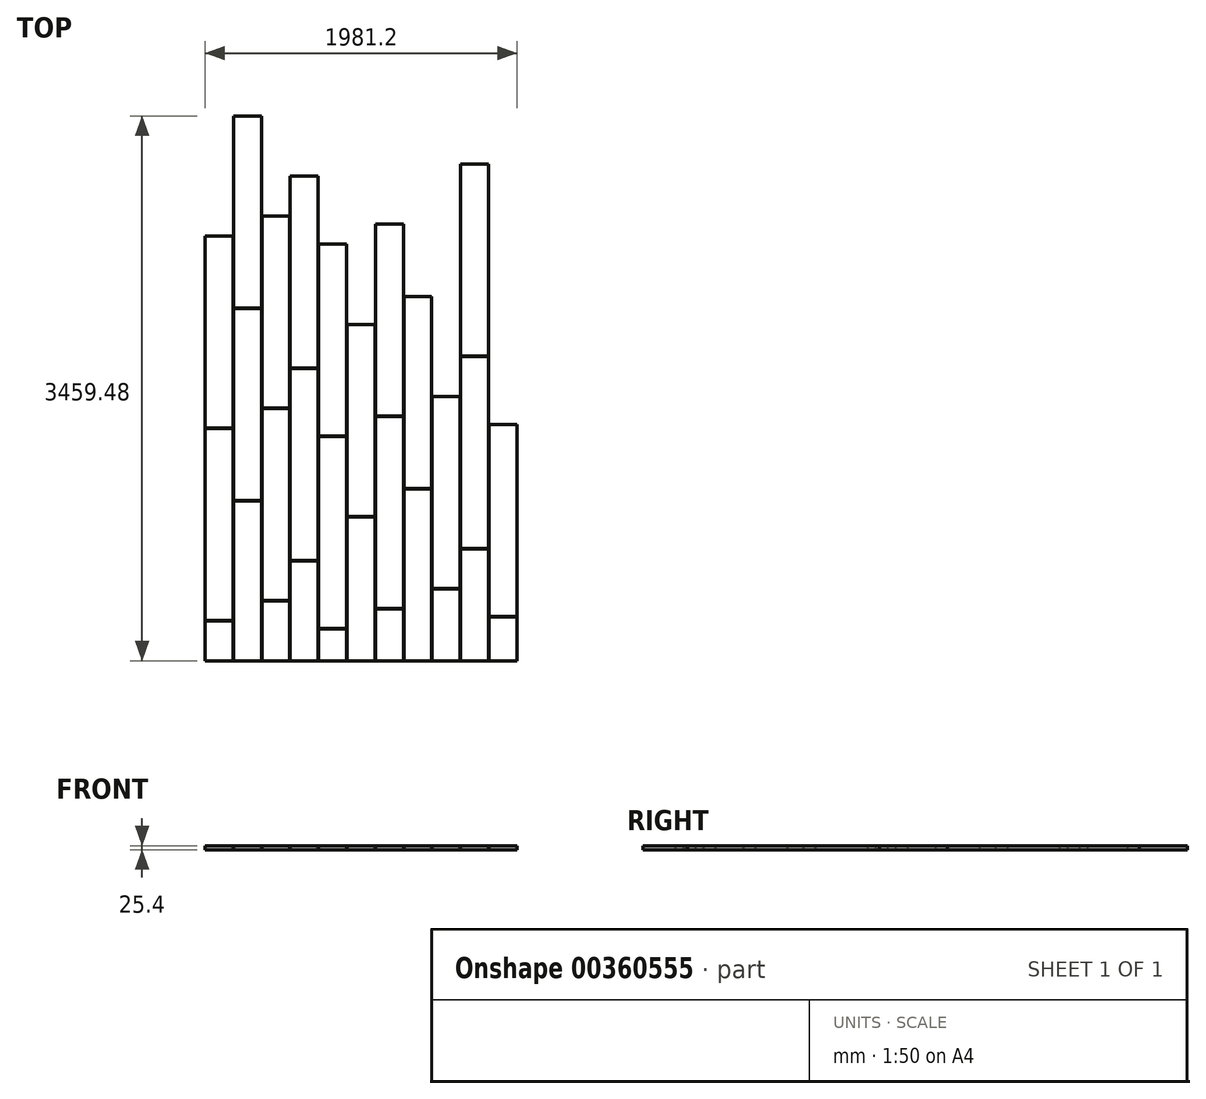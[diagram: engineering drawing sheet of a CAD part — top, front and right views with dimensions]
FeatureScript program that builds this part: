
annotation { "Feature Type Name" : "Feature", "Feature Type Description" : "" }
export const myFeature = defineFeature(function(context is Context, id is Id, definition is map)
    precondition{}
    {
        {
            var Q0;
            Q0=qCreatedBy(makeId("Top.planeOp"),FACE);
            var sketch = newSketch(context, id + "F0", { "sketchPlane" : qUnion([Q0])});
            skLineSegment(sketch, "E0.bottom", {"start": v(0, 0) * mm, "end": v(177.8, 0) * mm});
            skLineSegment(sketch, "E0.top", {"start": v(0, 254) * mm, "end": v(177.8, 254) * mm});
            skLineSegment(sketch, "E0.left", {"start": v(0, 0) * mm, "end": v(0, 254) * mm});
            skLineSegment(sketch, "E0.right", {"start": v(177.8, 0) * mm, "end": v(177.8, 254) * mm});
            skLineSegment(sketch, "E1.bottom", {"start": v(180.34, 0) * mm, "end": v(358.14, 0) * mm});
            skLineSegment(sketch, "E1.top", {"start": v(180.34, 1016) * mm, "end": v(358.14, 1016) * mm});
            skLineSegment(sketch, "E1.left", {"start": v(180.34, 0) * mm, "end": v(180.34, 1016) * mm});
            skLineSegment(sketch, "E1.right", {"start": v(358.14, 0) * mm, "end": v(358.14, 1016) * mm});
            skLineSegment(sketch, "E2.bottom", {"start": v(360.68, 0) * mm, "end": v(538.48, 0) * mm});
            skLineSegment(sketch, "E2.top", {"start": v(360.68, 381) * mm, "end": v(538.48, 381) * mm});
            skLineSegment(sketch, "E2.left", {"start": v(360.68, 0) * mm, "end": v(360.68, 381) * mm});
            skLineSegment(sketch, "E2.right", {"start": v(538.48, 0) * mm, "end": v(538.48, 381) * mm});
            skLineSegment(sketch, "E3.bottom", {"start": v(541.02, 0) * mm, "end": v(718.82, 0) * mm});
            skLineSegment(sketch, "E3.top", {"start": v(541.02, 635) * mm, "end": v(718.82, 635) * mm});
            skLineSegment(sketch, "E3.left", {"start": v(541.02, 0) * mm, "end": v(541.02, 635) * mm});
            skLineSegment(sketch, "E3.right", {"start": v(718.82, 0) * mm, "end": v(718.82, 635) * mm});
            skLineSegment(sketch, "E4.bottom", {"start": v(721.36, 0) * mm, "end": v(899.16, 0) * mm});
            skLineSegment(sketch, "E4.top", {"start": v(721.36, 203.2) * mm, "end": v(899.16, 203.2) * mm});
            skLineSegment(sketch, "E4.left", {"start": v(721.36, 0) * mm, "end": v(721.36, 203.2) * mm});
            skLineSegment(sketch, "E4.right", {"start": v(899.16, 0) * mm, "end": v(899.16, 203.2) * mm});
            skLineSegment(sketch, "E5.bottom", {"start": v(0, 256.54) * mm, "end": v(177.8, 256.54) * mm});
            skLineSegment(sketch, "E5.top", {"start": v(0, 1475.74) * mm, "end": v(177.8, 1475.74) * mm});
            skLineSegment(sketch, "E5.left", {"start": v(0, 256.54) * mm, "end": v(0, 1475.74) * mm});
            skLineSegment(sketch, "E5.right", {"start": v(177.8, 256.54) * mm, "end": v(177.8, 1475.74) * mm});
            skLineSegment(sketch, "E6.bottom", {"start": v(180.34, 1018.54) * mm, "end": v(358.14, 1018.54) * mm});
            skLineSegment(sketch, "E6.top", {"start": v(180.34, 2237.74) * mm, "end": v(358.14, 2237.74) * mm});
            skLineSegment(sketch, "E6.left", {"start": v(180.34, 1018.54) * mm, "end": v(180.34, 2237.74) * mm});
            skLineSegment(sketch, "E6.right", {"start": v(358.14, 1018.54) * mm, "end": v(358.14, 2237.74) * mm});
            skLineSegment(sketch, "E7.bottom", {"start": v(360.68, 383.54) * mm, "end": v(538.48, 383.54) * mm});
            skLineSegment(sketch, "E7.top", {"start": v(360.68, 1602.74) * mm, "end": v(538.48, 1602.74) * mm});
            skLineSegment(sketch, "E7.left", {"start": v(360.68, 383.54) * mm, "end": v(360.68, 1602.74) * mm});
            skLineSegment(sketch, "E7.right", {"start": v(538.48, 383.54) * mm, "end": v(538.48, 1602.74) * mm});
            skLineSegment(sketch, "E8.bottom", {"start": v(541.02, 637.54) * mm, "end": v(718.82, 637.54) * mm});
            skLineSegment(sketch, "E8.top", {"start": v(541.02, 1856.74) * mm, "end": v(718.82, 1856.74) * mm});
            skLineSegment(sketch, "E8.left", {"start": v(541.02, 637.54) * mm, "end": v(541.02, 1856.74) * mm});
            skLineSegment(sketch, "E8.right", {"start": v(718.82, 637.54) * mm, "end": v(718.82, 1856.74) * mm});
            skLineSegment(sketch, "E9.bottom", {"start": v(721.36, 205.74) * mm, "end": v(899.16, 205.74) * mm});
            skLineSegment(sketch, "E9.top", {"start": v(721.36, 1424.94) * mm, "end": v(899.16, 1424.94) * mm});
            skLineSegment(sketch, "E9.left", {"start": v(721.36, 205.74) * mm, "end": v(721.36, 1424.94) * mm});
            skLineSegment(sketch, "E9.right", {"start": v(899.16, 205.74) * mm, "end": v(899.16, 1424.94) * mm});
            skLineSegment(sketch, "E10.bottom", {"start": v(0, 1478.28) * mm, "end": v(177.8, 1478.28) * mm});
            skLineSegment(sketch, "E10.top", {"start": v(0, 2697.48) * mm, "end": v(177.8, 2697.48) * mm});
            skLineSegment(sketch, "E10.left", {"start": v(0, 1478.28) * mm, "end": v(0, 2697.48) * mm});
            skLineSegment(sketch, "E10.right", {"start": v(177.8, 1478.28) * mm, "end": v(177.8, 2697.48) * mm});
            skPoint(sketch, "E11.firstSnap0", {"position": v(180.34, 1628.14) * mm});
            skLineSegment(sketch, "E11.bottom", {"start": v(180.34, 2240.28) * mm, "end": v(358.14, 2240.28) * mm});
            skLineSegment(sketch, "E11.top", {"start": v(180.34, 3459.48) * mm, "end": v(358.14, 3459.48) * mm});
            skLineSegment(sketch, "E11.left", {"start": v(180.34, 2240.28) * mm, "end": v(180.34, 3459.48) * mm});
            skLineSegment(sketch, "E11.right", {"start": v(358.14, 2240.28) * mm, "end": v(358.14, 3459.48) * mm});
            skLineSegment(sketch, "E12.bottom", {"start": v(360.68, 1605.28) * mm, "end": v(538.48, 1605.28) * mm});
            skLineSegment(sketch, "E12.top", {"start": v(360.68, 2824.48) * mm, "end": v(538.48, 2824.48) * mm});
            skLineSegment(sketch, "E12.left", {"start": v(360.68, 1605.28) * mm, "end": v(360.68, 2824.48) * mm});
            skLineSegment(sketch, "E12.right", {"start": v(538.48, 1605.28) * mm, "end": v(538.48, 2824.48) * mm});
            skLineSegment(sketch, "E13.bottom", {"start": v(541.02, 1859.28) * mm, "end": v(718.82, 1859.28) * mm});
            skLineSegment(sketch, "E13.top", {"start": v(541.02, 3078.48) * mm, "end": v(718.82, 3078.48) * mm});
            skLineSegment(sketch, "E13.left", {"start": v(541.02, 1859.28) * mm, "end": v(541.02, 3078.48) * mm});
            skLineSegment(sketch, "E13.right", {"start": v(718.82, 1859.28) * mm, "end": v(718.82, 3078.48) * mm});
            skPoint(sketch, "E14.oppositeSnap0", {"position": v(899.16, 815.34) * mm});
            skLineSegment(sketch, "E14.bottom", {"start": v(721.36, 1427.48) * mm, "end": v(899.16, 1427.48) * mm});
            skLineSegment(sketch, "E14.top", {"start": v(721.36, 2646.68) * mm, "end": v(899.16, 2646.68) * mm});
            skLineSegment(sketch, "E14.left", {"start": v(721.36, 1427.48) * mm, "end": v(721.36, 2646.68) * mm});
            skLineSegment(sketch, "E14.right", {"start": v(899.16, 1427.48) * mm, "end": v(899.16, 2646.68) * mm});
            skLineSegment(sketch, "E15.bottom", {"start": v(901.7, 0) * mm, "end": v(1079.5, 0) * mm});
            skLineSegment(sketch, "E15.top", {"start": v(901.7, 914.4) * mm, "end": v(1079.5, 914.4) * mm});
            skLineSegment(sketch, "E15.left", {"start": v(901.7, 0) * mm, "end": v(901.7, 914.4) * mm});
            skLineSegment(sketch, "E15.right", {"start": v(1079.5, 0) * mm, "end": v(1079.5, 914.4) * mm});
            skLineSegment(sketch, "E16.bottom", {"start": v(901.7, 916.94) * mm, "end": v(1079.5, 916.94) * mm});
            skLineSegment(sketch, "E16.top", {"start": v(901.7, 2136.14) * mm, "end": v(1079.5, 2136.14) * mm});
            skLineSegment(sketch, "E16.left", {"start": v(901.7, 916.94) * mm, "end": v(901.7, 2136.14) * mm});
            skLineSegment(sketch, "E16.right", {"start": v(1079.5, 916.94) * mm, "end": v(1079.5, 2136.14) * mm});
            skLineSegment(sketch, "E17.bottom", {"start": v(1082.04, 0) * mm, "end": v(1259.84, 0) * mm});
            skLineSegment(sketch, "E17.top", {"start": v(1082.04, 330.2) * mm, "end": v(1259.84, 330.2) * mm});
            skLineSegment(sketch, "E17.left", {"start": v(1082.04, 0) * mm, "end": v(1082.04, 330.2) * mm});
            skLineSegment(sketch, "E17.right", {"start": v(1259.84, 0) * mm, "end": v(1259.84, 330.2) * mm});
            skLineSegment(sketch, "E18.bottom", {"start": v(1262.38, 0) * mm, "end": v(1440.18, 0) * mm});
            skLineSegment(sketch, "E18.top", {"start": v(1262.38, 1092.2) * mm, "end": v(1440.18, 1092.2) * mm});
            skLineSegment(sketch, "E18.left", {"start": v(1262.38, 0) * mm, "end": v(1262.38, 1092.2) * mm});
            skLineSegment(sketch, "E18.right", {"start": v(1440.18, 0) * mm, "end": v(1440.18, 1092.2) * mm});
            skLineSegment(sketch, "E19.bottom", {"start": v(1082.04, 332.74) * mm, "end": v(1259.84, 332.74) * mm});
            skLineSegment(sketch, "E19.top", {"start": v(1082.04, 1551.94) * mm, "end": v(1259.84, 1551.94) * mm});
            skLineSegment(sketch, "E19.left", {"start": v(1082.04, 332.74) * mm, "end": v(1082.04, 1551.94) * mm});
            skLineSegment(sketch, "E19.right", {"start": v(1259.84, 332.74) * mm, "end": v(1259.84, 1551.94) * mm});
            skLineSegment(sketch, "E20.bottom", {"start": v(1442.72, 0) * mm, "end": v(1620.52, 0) * mm});
            skLineSegment(sketch, "E20.top", {"start": v(1442.72, 457.2) * mm, "end": v(1620.52, 457.2) * mm});
            skLineSegment(sketch, "E20.left", {"start": v(1442.72, 0) * mm, "end": v(1442.72, 457.2) * mm});
            skLineSegment(sketch, "E20.right", {"start": v(1620.52, 0) * mm, "end": v(1620.52, 457.2) * mm});
            skLineSegment(sketch, "E21.bottom", {"start": v(1623.06, 0) * mm, "end": v(1800.86, 0) * mm});
            skLineSegment(sketch, "E21.top", {"start": v(1623.06, 711.2) * mm, "end": v(1800.86, 711.2) * mm});
            skLineSegment(sketch, "E21.left", {"start": v(1623.06, 0) * mm, "end": v(1623.06, 711.2) * mm});
            skLineSegment(sketch, "E21.right", {"start": v(1800.86, 0) * mm, "end": v(1800.86, 711.2) * mm});
            skLineSegment(sketch, "E22.bottom", {"start": v(1442.72, 459.74) * mm, "end": v(1620.52, 459.74) * mm});
            skLineSegment(sketch, "E22.top", {"start": v(1442.72, 1678.94) * mm, "end": v(1620.52, 1678.94) * mm});
            skLineSegment(sketch, "E22.left", {"start": v(1442.72, 459.74) * mm, "end": v(1442.72, 1678.94) * mm});
            skLineSegment(sketch, "E22.right", {"start": v(1620.52, 459.74) * mm, "end": v(1620.52, 1678.94) * mm});
            skLineSegment(sketch, "E23.bottom", {"start": v(1623.06, 713.74) * mm, "end": v(1800.86, 713.74) * mm});
            skLineSegment(sketch, "E23.top", {"start": v(1623.06, 1932.94) * mm, "end": v(1800.86, 1932.94) * mm});
            skLineSegment(sketch, "E23.left", {"start": v(1623.06, 713.74) * mm, "end": v(1623.06, 1932.94) * mm});
            skLineSegment(sketch, "E23.right", {"start": v(1800.86, 713.74) * mm, "end": v(1800.86, 1932.94) * mm});
            skLineSegment(sketch, "E24.bottom", {"start": v(1082.04, 1554.48) * mm, "end": v(1259.84, 1554.48) * mm});
            skLineSegment(sketch, "E24.top", {"start": v(1082.04, 2773.68) * mm, "end": v(1259.84, 2773.68) * mm});
            skLineSegment(sketch, "E24.left", {"start": v(1082.04, 1554.48) * mm, "end": v(1082.04, 2773.68) * mm});
            skLineSegment(sketch, "E24.right", {"start": v(1259.84, 1554.48) * mm, "end": v(1259.84, 2773.68) * mm});
            skLineSegment(sketch, "E25.bottom", {"start": v(1262.38, 1094.74) * mm, "end": v(1440.18, 1094.74) * mm});
            skLineSegment(sketch, "E25.top", {"start": v(1262.38, 2313.94) * mm, "end": v(1440.18, 2313.94) * mm});
            skLineSegment(sketch, "E25.left", {"start": v(1262.38, 1094.74) * mm, "end": v(1262.38, 2313.94) * mm});
            skLineSegment(sketch, "E25.right", {"start": v(1440.18, 1094.74) * mm, "end": v(1440.18, 2313.94) * mm});
            skLineSegment(sketch, "E26.bottom", {"start": v(1623.06, 1935.48) * mm, "end": v(1800.86, 1935.48) * mm});
            skLineSegment(sketch, "E26.top", {"start": v(1623.06, 3154.68) * mm, "end": v(1800.86, 3154.68) * mm});
            skLineSegment(sketch, "E26.left", {"start": v(1623.06, 1935.48) * mm, "end": v(1623.06, 3154.68) * mm});
            skLineSegment(sketch, "E26.right", {"start": v(1800.86, 1935.48) * mm, "end": v(1800.86, 3154.68) * mm});
            skLineSegment(sketch, "E27.bottom", {"start": v(1803.4, 0) * mm, "end": v(1981.2, 0) * mm});
            skLineSegment(sketch, "E27.top", {"start": v(1803.4, 279.4) * mm, "end": v(1981.2, 279.4) * mm});
            skLineSegment(sketch, "E27.left", {"start": v(1803.4, 0) * mm, "end": v(1803.4, 279.4) * mm});
            skLineSegment(sketch, "E27.right", {"start": v(1981.2, 0) * mm, "end": v(1981.2, 279.4) * mm});
            skLineSegment(sketch, "E28.bottom", {"start": v(1803.4, 281.94) * mm, "end": v(1981.2, 281.94) * mm});
            skLineSegment(sketch, "E28.top", {"start": v(1803.4, 1501.14) * mm, "end": v(1981.2, 1501.14) * mm});
            skLineSegment(sketch, "E28.left", {"start": v(1803.4, 281.94) * mm, "end": v(1803.4, 1501.14) * mm});
            skLineSegment(sketch, "E28.right", {"start": v(1981.2, 281.94) * mm, "end": v(1981.2, 1501.14) * mm});
            skSolve(sketch);
        }
        {
            var Q0;
            Q0 = qSketchRegion(id + "F0", true);
            extrude(context, id + "F1", {"entities" : qUnion([Q0]), "depth" : 25.4 * mm});
        }
    });
